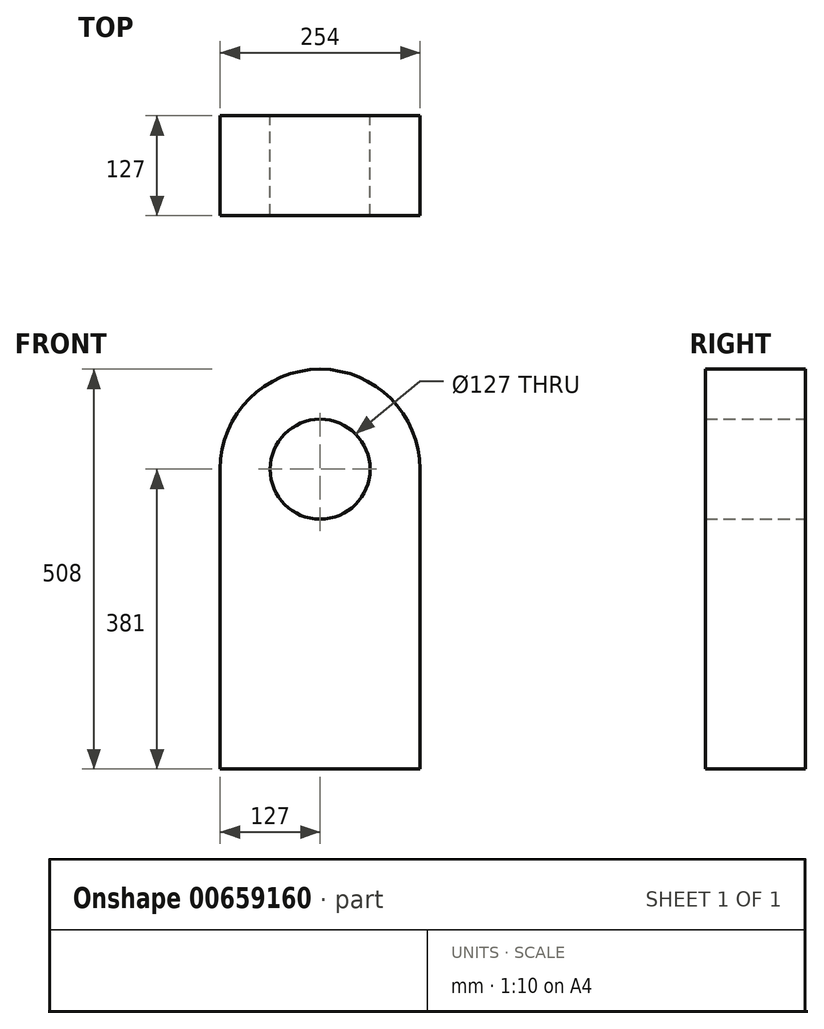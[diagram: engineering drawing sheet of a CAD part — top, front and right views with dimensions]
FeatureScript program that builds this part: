
annotation { "Feature Type Name" : "Feature", "Feature Type Description" : "" }
export const myFeature = defineFeature(function(context is Context, id is Id, definition is map)
    precondition{}
    {
        {
            var Q0;
            Q0=qCreatedBy(makeId("Front.planeOp"),FACE);
            var sketch = newSketch(context, id + "F0", { "sketchPlane" : qUnion([Q0])});
            skLineSegment(sketch, "E0.top", {"start": v(-127, -254) * mm, "end": v(127, -254) * mm});
            skLineSegment(sketch, "E0.left", {"start": v(-127, 127) * mm, "end": v(-127, -254) * mm});
            skLineSegment(sketch, "E0.right", {"start": v(127, 127) * mm, "end": v(127, -254) * mm});
            skPoint(sketch, "E0.middle", {"position": v(0, 0) * mm});
            skArc(sketch, "E1", {"start": v(127, 127) * mm, "mid": v(0, 254) * mm, "end": v(-127, 127) * mm});
            skPoint(sketch, "E2.orphan", {"position": v(-127, 254) * mm});
            skPoint(sketch, "E3.orphan", {"position": v(127, 254) * mm});
            skCircle(sketch, "E4", {"center": v(0, 127) * mm, "radius": 63.5 * mm});
            skSolve(sketch);
        }
        {
            var Q0;
            Q0=makeQuery(id+"F0.imprint","IMPRINT",FACE,{"disambiguationData":[TD([[makeQuery(id+"F0.imprint","IMPRINT",EDGE,{"derivedFrom":sQuery(id+"F0.wireOp",EDGE,"E0.top")}),1.0]])]});
            extrude(context, id + "F1", {"entities" : qUnion([Q0]), "depth" : 127 * mm, "offsetDistance" : 25.4 * mm});
        }
    });
